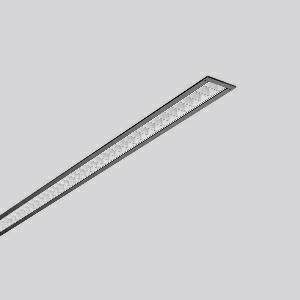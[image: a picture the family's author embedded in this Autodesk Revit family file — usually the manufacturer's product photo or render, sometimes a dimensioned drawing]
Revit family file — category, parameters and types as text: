
# Revit family: less_is_more_27_312179_003_1_76_1901
name_source: partatom
category: Lighting Fixtures
units: mm (PartAtom-declared; Revit-internal decimal feet)

## family parameters
Cut with Voids When Loaded = No
Host = Face
Light Source = No
Part Type = Normal
Room Calculation Point = No
Round Connector Dimension = Use Diameter
Shared = No

## types (1)
- LESS IS MORE 27 (1 x LED Modul 840, 3500 lm, 4000)
    Apparent Load = 39 VA
    CIE Flux Codes = 90 99 100 100 100
    Color Rendering = 80
    Color Temperature = 4000
    Default Elevation = 1800 mm
    Description = Series: LESS IS MORE 27
Recessed ceiling and wall luminaire with slim design. Housing: extruded aluminium profile, powder-coated. End cap aluminium powder-coated. High polish aluminium micro grid. Perfect for office areas (RUG < 19) and environments with computer screens in accordance with EN 12464-1. Suitable for Recessed ceiling mounting, wall (recessed). External driver with connecting cable. 
Colour: deep black, matt (RAL 9005)
Length: 1514 mm
Width: 38 mm
Height: 2 mm
Cut-out length: 1506 mm
Cut-out width: 30 mm
Recess height: 45-60 mm
Luminaire: recess height: 37 mm
Lamp: LED
Socket: without socket
Colour temperature: 4000K
Colour rendering index (CRI): 82
System power: 39 W
Rated luminous flux: 3500 lm
Luminous efficiency: 90 lm/W
Control gear: Voltage converter, DALI dim.
Protection class: II
Type of protection: IP 20
    Height = 0 mm  [stored 0 ft]
    Lamp = 1 x LED Modul 840
    Lamp Light Flux = 3500 lm
    Lamp count = 1
    Length = 1514 mm
    Lifetime = 50000 h
    Luminous efficacy = 90 lm/W
    Manufacturer = RZB
    ModVariant = No
    Model = 312179.003.1.76
    Mounting Place = Ceiling, Wall
    Mounting Type = Recessed
    Number of Poles = 1
    OnlyDefault = Yes
    Power Factor = 1
    Product Name = LESS IS MORE 27
    Product group = Recessed LED linear luminaires
    ProductGroupID = 407
    Protection Class = Protection class II
    Protection Degree = IP 20
    RLX_Detail_Level = 1
    RLX_Emergency_Light_Flux = 0 lm
    RLX_Emergency_Type = 0
    RLX_Emergency_Type_DB = No
    RlxData = <blob elided: 29917 chars, md5=58599387>
    Socket = socket
    Standby Power = 0 W
    System Light Flux = 3500 lm
    System Power = 39 W
    Type Comments = Product without accessories
    Type Image = 312177.003.jpg
    URL = http://relux.com
    VarID = ---
    Voltage = 230 V
    Voltage Range = 220-240 V
    Weight = 0.00 kg
    Width = 38 mm

note: [stored X ft] marks values corroborated as IEEE doubles in the binary element streams (Revit-internal decimal feet)

## geometry (parser evidence)
native form markers: Blend x4, Sweep x11
no freeform markers — native parametric forms only
